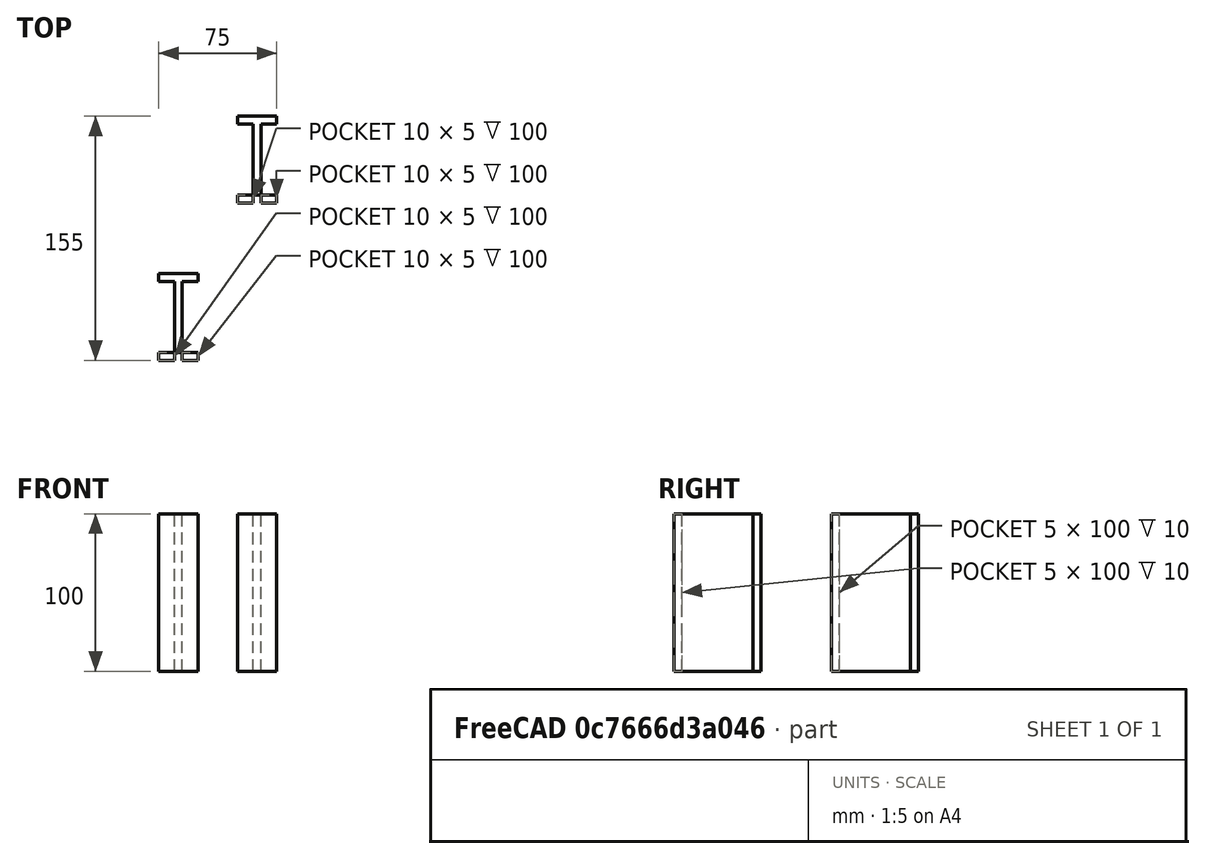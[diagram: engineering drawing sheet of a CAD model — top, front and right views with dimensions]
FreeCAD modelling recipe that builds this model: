
FCSTD DOCUMENT  (FreeCAD 0.19R)
Label: VIGA-MATEMATICA-01
License: Creative Commons Attribution-NonCommercial
LicenseURL: http://creativecommons.org/licenses/by-nc/4.0/
objects: Sketcher::SketchObject×2, Part::Extrusion×2, Spreadsheet::Sheet×1
note: 4 computed .brp shape members not serialized (recipe doc carries the construction recipe); baked Part::Feature solids carry a one-line shape summary decoded from their .brp

FEATURE [Spreadsheet::Sheet] Spreadsheet
  cells = A2=Altura; B2=Largura; C2=Espessura; D2=Comprimento; E2=posicao X; F2=posicao Y; A3(altura1)=50; B3(largura1)==0.5 * altura1; C3(espessura1)==0.1 * altura1; D3(comprimento1)=100; E3(x1)=50; F3(y1)=100; A4(altura2)==2 * altura1; B4(largura2)==0.5 * altura1; C4(espessura2)==0.1 * altura1; D4(comprimento2)=100; E4(x2)=100; F4(y2)=200
FEATURE [Sketcher::SketchObject] Sketch
  expr: Constraints[56] = Spreadsheet.espessura1
  expr: Constraints[52] = Spreadsheet.x1
  expr: Constraints[55] = Spreadsheet.altura1
  expr: Constraints[53] = Spreadsheet.y1
  expr: Constraints[54] = Spreadsheet.largura1
  sketch-geometry (20):
    g0: LineSegment StartX=37.5 StartY=125 StartZ=0 EndX=62.5 EndY=125 EndZ=0
    g1: LineSegment StartX=62.5 StartY=125 StartZ=0 EndX=62.5 EndY=120 EndZ=0
    g2: LineSegment StartX=37.5 StartY=120 StartZ=0 EndX=37.5 EndY=125 EndZ=0
    g3: LineSegment StartX=62.5 StartY=120 StartZ=0 EndX=52.5 EndY=120 EndZ=0
    g4: LineSegment StartX=52.5 StartY=120 StartZ=0 EndX=52.5 EndY=70 EndZ=0
    g5: LineSegment StartX=47.5 StartY=70 StartZ=0 EndX=47.5 EndY=120 EndZ=0
    g6: LineSegment StartX=62.5 StartY=70 StartZ=0 EndX=62.5 EndY=75 EndZ=0
    g7: LineSegment StartX=62.5 StartY=75 StartZ=0 EndX=37.5 EndY=75 EndZ=0
    g8: LineSegment StartX=37.5 StartY=75 StartZ=0 EndX=37.5 EndY=70 EndZ=0
    g9: LineSegment [constr] StartX=37.5 StartY=120 StartZ=0 EndX=37.5 EndY=70 EndZ=0
    g10: LineSegment [constr] StartX=62.5 StartY=120 StartZ=0 EndX=62.5 EndY=70 EndZ=0
    g11: LineSegment StartX=47.5 StartY=120 StartZ=0 EndX=37.5 EndY=120 EndZ=0
    g12: LineSegment StartX=37.5 StartY=70 StartZ=0 EndX=47.5 EndY=70 EndZ=0
    g13: LineSegment [constr] StartX=47.5 StartY=70 StartZ=0 EndX=52.5 EndY=70 EndZ=0
    g14: LineSegment StartX=52.5 StartY=70 StartZ=0 EndX=62.5 EndY=70 EndZ=0
    g15: LineSegment [constr] StartX=47.5 StartY=120 StartZ=0 EndX=52.5 EndY=120 EndZ=0
    g16: LineSegment [constr] StartX=50 StartY=125 StartZ=0 EndX=50 EndY=100 EndZ=0
    g17: LineSegment [constr] StartX=50 StartY=100 StartZ=0 EndX=50 EndY=75 EndZ=0
    g18: LineSegment [constr] StartX=37.5 StartY=100 StartZ=0 EndX=50 EndY=100 EndZ=0
    g19: LineSegment [constr] StartX=50 StartY=100 StartZ=0 EndX=62.5 EndY=100 EndZ=0
  constraints (57):
    c: Coincident(g0,g1)
    c: Coincident(g11,g2)
    c: Coincident(g2,g0)
    c: Horizontal(g0)
    c: Vertical(g1)
    c: Vertical(g2)
    c: Coincident(g3,g4)
    c: Horizontal(g3)
    c: Vertical(g4)
    c: Vertical(g5)
    c: Coincident(g6,g7)
    c: Coincident(g7,g8)
    c: Horizontal(g7)
    c: Vertical(g6)
    c: Vertical(g8)
    c: Coincident(g9,g11)
    c: Vertical(g9)
    c: Coincident(g10,g1)
    c: Vertical(g10)
    c: Coincident(g1,g3)
    c: Coincident(g8,g12)
    c: Coincident(g12,g5)
    c: Horizontal(g12)
    c: Coincident(g12,g13)
    c: Coincident(g13,g4)
    c: Horizontal(g13)
    c: Coincident(g13,g14)
    c: Coincident(g14,g6)
    c: Horizontal(g14)
    c: Coincident(g15,g11)
    c: Coincident(g15,g3)
    c: Horizontal(g15)
    c: PointOnObject(g16,g0)
    c: Vertical(g16)
    c: Coincident(g16,g17)
    c: PointOnObject(g17,g7)
    c: Vertical(g17)
    c: PointOnObject(g18,g9)
    c: Coincident(g18,g16)
    c: Coincident(g18,g19)
    c: PointOnObject(g19,g10)
    c: Horizontal(g19)
    c: Horizontal(g18)
    c: Equal(g19,g18)
    c: Equal(g3,g11)
    c: Coincident(g5,g11)
    c: Coincident(g6,g10)
    c: Coincident(g8,g9)
    c: Equal(g1,g15)
    c: Horizontal(g11)
    c: Equal(g1,g6)
    c: Equal(g16,g17)
    c: DistanceX(g16) = 50
    c: DistanceY(g16) = 100
    c: DistanceX(g0,g0) = 25
    c: DistanceY(g6,g0) = 50
    c: DistanceY(g1,g1) = 5
FEATURE [Part::Extrusion] Extrude
  Base = -> Sketch
  Dir = (0,0,1)
  DirMode = 2
  FaceMakerClass = Part::FaceMakerBullseye
  LengthFwd = 100
  LengthRev = 0
  Solid = true
  Symmetric = false
  expr: LengthFwd = Spreadsheet.comprimento1
FEATURE [Sketcher::SketchObject] Sketch001
  expr: Constraints[55] = Sketch.Constraints[55]
  expr: Constraints[54] = Sketch.Constraints[54]
  expr: Constraints[53] = Spreadsheet.y2
  expr: Constraints[56] = Sketch.Constraints[56]
  expr: Constraints[52] = Spreadsheet.x2
  sketch-geometry (20):
    g0: LineSegment StartX=87.5 StartY=225 StartZ=0 EndX=112.5 EndY=225 EndZ=0
    g1: LineSegment StartX=112.5 StartY=225 StartZ=0 EndX=112.5 EndY=220 EndZ=0
    g2: LineSegment StartX=87.5 StartY=220 StartZ=0 EndX=87.5 EndY=225 EndZ=0
    g3: LineSegment StartX=112.5 StartY=220 StartZ=0 EndX=102.5 EndY=220 EndZ=0
    g4: LineSegment StartX=102.5 StartY=220 StartZ=0 EndX=102.5 EndY=170 EndZ=0
    g5: LineSegment StartX=97.5 StartY=170 StartZ=0 EndX=97.5 EndY=220 EndZ=0
    g6: LineSegment StartX=112.5 StartY=170 StartZ=0 EndX=112.5 EndY=175 EndZ=0
    g7: LineSegment StartX=112.5 StartY=175 StartZ=0 EndX=87.5 EndY=175 EndZ=0
    g8: LineSegment StartX=87.5 StartY=175 StartZ=0 EndX=87.5 EndY=170 EndZ=0
    g9: LineSegment [constr] StartX=87.5 StartY=220 StartZ=0 EndX=87.5 EndY=170 EndZ=0
    g10: LineSegment [constr] StartX=112.5 StartY=220 StartZ=0 EndX=112.5 EndY=170 EndZ=0
    g11: LineSegment StartX=97.5 StartY=220 StartZ=0 EndX=87.5 EndY=220 EndZ=0
    g12: LineSegment StartX=87.5 StartY=170 StartZ=0 EndX=97.5 EndY=170 EndZ=0
    g13: LineSegment [constr] StartX=97.5 StartY=170 StartZ=0 EndX=102.5 EndY=170 EndZ=0
    g14: LineSegment StartX=102.5 StartY=170 StartZ=0 EndX=112.5 EndY=170 EndZ=0
    g15: LineSegment [constr] StartX=97.5 StartY=220 StartZ=0 EndX=102.5 EndY=220 EndZ=0
    g16: LineSegment [constr] StartX=100 StartY=225 StartZ=0 EndX=100 EndY=200 EndZ=0
    g17: LineSegment [constr] StartX=100 StartY=200 StartZ=0 EndX=100 EndY=175 EndZ=0
    g18: LineSegment [constr] StartX=87.5 StartY=200 StartZ=0 EndX=100 EndY=200 EndZ=0
    g19: LineSegment [constr] StartX=100 StartY=200 StartZ=0 EndX=112.5 EndY=200 EndZ=0
  constraints (57):
    c: Coincident(g0,g1)
    c: Coincident(g11,g2)
    c: Coincident(g2,g0)
    c: Horizontal(g0)
    c: Vertical(g1)
    c: Vertical(g2)
    c: Coincident(g3,g4)
    c: Horizontal(g3)
    c: Vertical(g4)
    c: Vertical(g5)
    c: Coincident(g6,g7)
    c: Coincident(g7,g8)
    c: Horizontal(g7)
    c: Vertical(g6)
    c: Vertical(g8)
    c: Coincident(g9,g11)
    c: Vertical(g9)
    c: Coincident(g10,g1)
    c: Vertical(g10)
    c: Coincident(g1,g3)
    c: Coincident(g8,g12)
    c: Coincident(g12,g5)
    c: Horizontal(g12)
    c: Coincident(g12,g13)
    c: Coincident(g13,g4)
    c: Horizontal(g13)
    c: Coincident(g13,g14)
    c: Coincident(g14,g6)
    c: Horizontal(g14)
    c: Coincident(g15,g11)
    c: Coincident(g15,g3)
    c: Horizontal(g15)
    c: PointOnObject(g16,g0)
    c: Vertical(g16)
    c: Coincident(g16,g17)
    c: PointOnObject(g17,g7)
    c: Vertical(g17)
    c: PointOnObject(g18,g9)
    c: Coincident(g18,g16)
    c: Coincident(g18,g19)
    c: PointOnObject(g19,g10)
    c: Horizontal(g19)
    c: Horizontal(g18)
    c: Equal(g19,g18)
    c: Equal(g3,g11)
    c: Coincident(g5,g11)
    c: Coincident(g6,g10)
    c: Coincident(g8,g9)
    c: Equal(g1,g15)
    c: Horizontal(g11)
    c: Equal(g1,g6)
    c: Equal(g16,g17)
    c: DistanceX(g16) = 100
    c: DistanceY(g16) = 200
    c: DistanceX(g0,g0) = 25
    c: DistanceY(g6,g0) = 50
    c: DistanceY(g1,g1) = 5
FEATURE [Part::Extrusion] Extrude001
  Base = -> Sketch001
  Dir = (0,0,1)
  DirMode = 2
  FaceMakerClass = Part::FaceMakerBullseye
  LengthFwd = 100
  LengthRev = 0
  Solid = true
  Symmetric = false
  expr: LengthFwd = Spreadsheet.altura2
